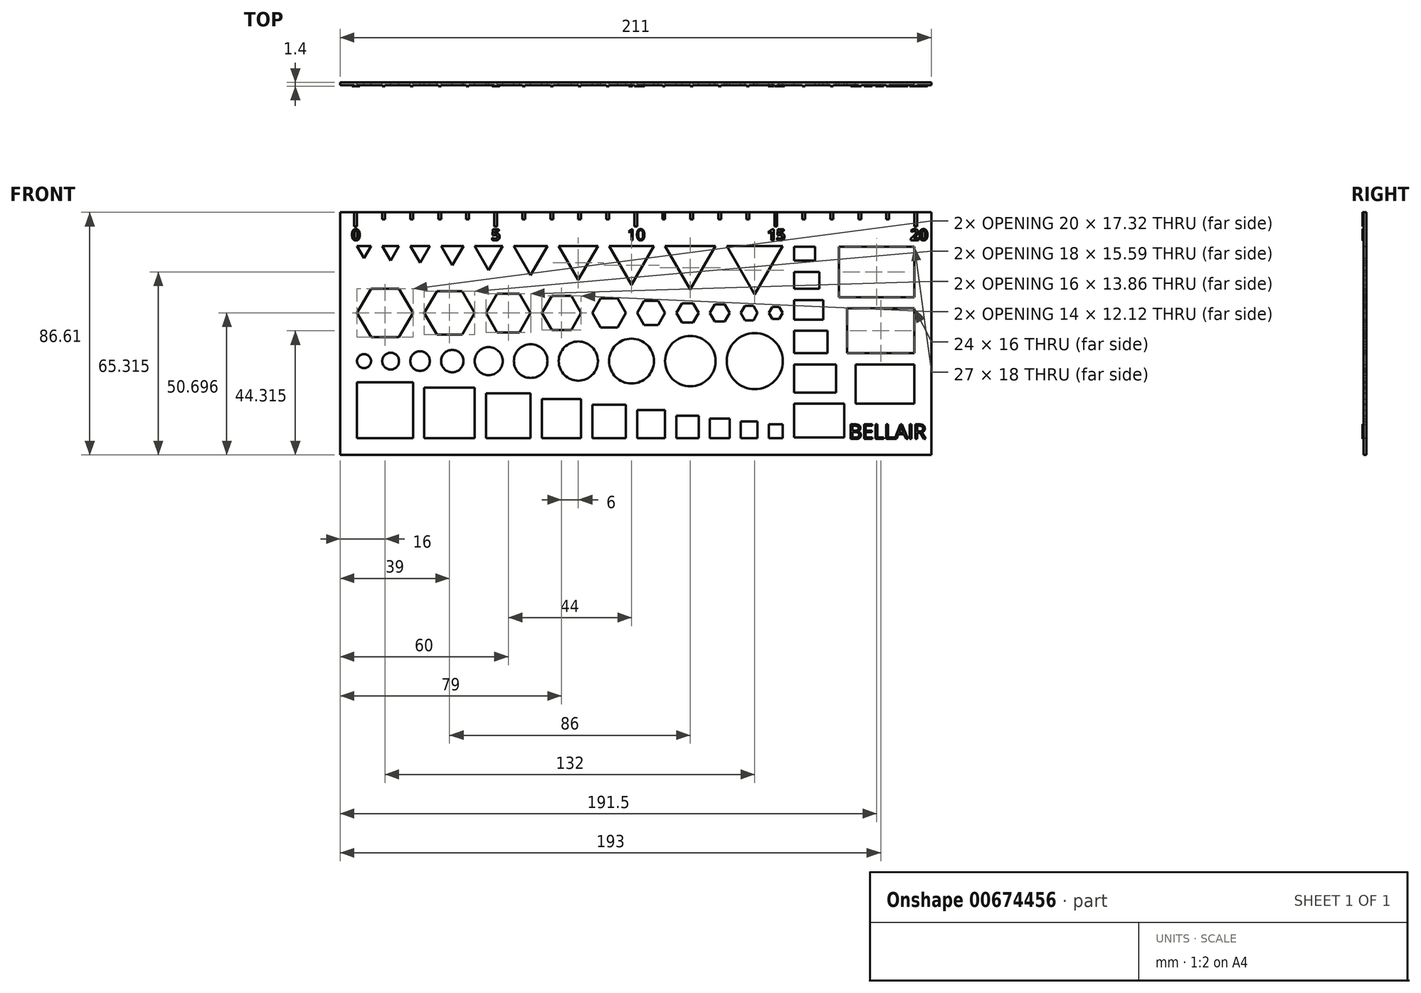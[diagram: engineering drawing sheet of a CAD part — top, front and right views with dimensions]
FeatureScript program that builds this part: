
annotation { "Feature Type Name" : "Feature", "Feature Type Description" : "" }
export const myFeature = defineFeature(function(context is Context, id is Id, definition is map)
    precondition{}
    {
        {
            var Q0;
            Q0=qCreatedBy(makeId("Front.planeOp"),FACE);
            var sketch = newSketch(context, id + "F0", { "sketchPlane" : qUnion([Q0])});
            skLineSegment(sketch, "E0.bottom", {"start": v(0, 0) * mm, "end": v(20, 0) * mm});
            skLineSegment(sketch, "E0.top", {"start": v(0, 20) * mm, "end": v(20, 20) * mm});
            skLineSegment(sketch, "E0.left", {"start": v(0, 0) * mm, "end": v(0, 20) * mm});
            skLineSegment(sketch, "E0.right", {"start": v(20, 0) * mm, "end": v(20, 20) * mm});
            skLineSegment(sketch, "E1.bottom", {"start": v(24, 0) * mm, "end": v(42, 0) * mm});
            skLineSegment(sketch, "E1.top", {"start": v(24, 18) * mm, "end": v(42, 18) * mm});
            skLineSegment(sketch, "E1.left", {"start": v(24, 0) * mm, "end": v(24, 18) * mm});
            skLineSegment(sketch, "E1.right", {"start": v(42, 0) * mm, "end": v(42, 18) * mm});
            skLineSegment(sketch, "E2.bottom", {"start": v(46, 0) * mm, "end": v(62, 0) * mm});
            skLineSegment(sketch, "E2.top", {"start": v(46, 16) * mm, "end": v(62, 16) * mm});
            skLineSegment(sketch, "E2.left", {"start": v(46, 0) * mm, "end": v(46, 16) * mm});
            skLineSegment(sketch, "E2.right", {"start": v(62, 0) * mm, "end": v(62, 16) * mm});
            skLineSegment(sketch, "E3.bottom", {"start": v(66, 0) * mm, "end": v(80, 0) * mm});
            skLineSegment(sketch, "E3.top", {"start": v(66, 14) * mm, "end": v(80, 14) * mm});
            skLineSegment(sketch, "E3.left", {"start": v(66, 0) * mm, "end": v(66, 14) * mm});
            skLineSegment(sketch, "E3.right", {"start": v(80, 0) * mm, "end": v(80, 14) * mm});
            skLineSegment(sketch, "E4.bottom", {"start": v(84, 0) * mm, "end": v(96, 0) * mm});
            skLineSegment(sketch, "E4.top", {"start": v(84, 12) * mm, "end": v(96, 12) * mm});
            skLineSegment(sketch, "E4.left", {"start": v(84, 0) * mm, "end": v(84, 12) * mm});
            skLineSegment(sketch, "E4.right", {"start": v(96, 0) * mm, "end": v(96, 12) * mm});
            skLineSegment(sketch, "E5.bottom", {"start": v(100, 0) * mm, "end": v(110, 0) * mm});
            skLineSegment(sketch, "E5.top", {"start": v(100, 10) * mm, "end": v(110, 10) * mm});
            skLineSegment(sketch, "E5.left", {"start": v(100, 0) * mm, "end": v(100, 10) * mm});
            skLineSegment(sketch, "E5.right", {"start": v(110, 0) * mm, "end": v(110, 10) * mm});
            skLineSegment(sketch, "E6.bottom", {"start": v(114, 0) * mm, "end": v(122, 0) * mm});
            skLineSegment(sketch, "E6.top", {"start": v(114, 8) * mm, "end": v(122, 8) * mm});
            skLineSegment(sketch, "E6.left", {"start": v(114, 0) * mm, "end": v(114, 8) * mm});
            skLineSegment(sketch, "E6.right", {"start": v(122, 0) * mm, "end": v(122, 8) * mm});
            skLineSegment(sketch, "E7.bottom", {"start": v(126, 0) * mm, "end": v(133, 0) * mm});
            skLineSegment(sketch, "E7.top", {"start": v(126, 7) * mm, "end": v(133, 7) * mm});
            skLineSegment(sketch, "E7.left", {"start": v(126, 0) * mm, "end": v(126, 7) * mm});
            skLineSegment(sketch, "E7.right", {"start": v(133, 0) * mm, "end": v(133, 7) * mm});
            skLineSegment(sketch, "E8.bottom", {"start": v(137, 0) * mm, "end": v(143, 0) * mm});
            skLineSegment(sketch, "E8.top", {"start": v(137, 6) * mm, "end": v(143, 6) * mm});
            skLineSegment(sketch, "E8.left", {"start": v(137, 0) * mm, "end": v(137, 6) * mm});
            skLineSegment(sketch, "E8.right", {"start": v(143, 0) * mm, "end": v(143, 6) * mm});
            skLineSegment(sketch, "E9.bottom", {"start": v(147, 0) * mm, "end": v(152, 0) * mm});
            skLineSegment(sketch, "E9.top", {"start": v(147, 5) * mm, "end": v(152, 5) * mm});
            skLineSegment(sketch, "E9.left", {"start": v(147, 0) * mm, "end": v(147, 5) * mm});
            skLineSegment(sketch, "E9.right", {"start": v(152, 0) * mm, "end": v(152, 5) * mm});
            skCircle(sketch, "E10", {"center": v(2.5, 27.5) * mm, "radius": 2.5 * mm});
            skCircle(sketch, "E11", {"center": v(12, 27.5) * mm, "radius": 3 * mm});
            skCircle(sketch, "E12", {"center": v(22.5, 27.5) * mm, "radius": 3.5 * mm});
            skCircle(sketch, "E13", {"center": v(34, 27.5) * mm, "radius": 4 * mm});
            skCircle(sketch, "E14", {"center": v(47, 27.5) * mm, "radius": 5 * mm});
            skCircle(sketch, "E15", {"center": v(62, 27.5) * mm, "radius": 6 * mm});
            skCircle(sketch, "E16", {"center": v(79, 27.5) * mm, "radius": 7 * mm});
            skCircle(sketch, "E17", {"center": v(98, 27.5) * mm, "radius": 8 * mm});
            skCircle(sketch, "E18", {"center": v(119, 27.5) * mm, "radius": 9 * mm});
            skCircle(sketch, "E19", {"center": v(142, 27.5) * mm, "radius": 10 * mm});
            skCircle(sketch, "E20.cCircle", {"center": v(10, 44.7) * mm, "radius": 8.66 * mm, "construction": true});
            skLineSegment(sketch, "E20.0", {"start": v(5, 53.36) * mm, "end": v(15, 53.36) * mm});
            skLineSegment(sketch, "E20.1", {"start": v(15, 53.36) * mm, "end": v(20, 44.7) * mm});
            skLineSegment(sketch, "E20.2", {"start": v(20, 44.7) * mm, "end": v(15, 36.04) * mm});
            skLineSegment(sketch, "E20.3", {"start": v(15, 36.04) * mm, "end": v(5, 36.04) * mm});
            skLineSegment(sketch, "E20.4", {"start": v(5, 36.04) * mm, "end": v(0, 44.7) * mm});
            skLineSegment(sketch, "E20.5", {"start": v(0, 44.7) * mm, "end": v(5, 53.36) * mm});
            skPoint(sketch, "E20.0.midPoint", {"position": v(10, 53.36) * mm});
            skCircle(sketch, "E21.cCircle", {"center": v(33, 44.7) * mm, "radius": 7.8 * mm, "construction": true});
            skLineSegment(sketch, "E21.0", {"start": v(37.5, 36.9) * mm, "end": v(28.5, 36.9) * mm});
            skLineSegment(sketch, "E21.1", {"start": v(28.5, 36.9) * mm, "end": v(24, 44.7) * mm});
            skLineSegment(sketch, "E21.2", {"start": v(24, 44.7) * mm, "end": v(28.5, 52.5) * mm});
            skLineSegment(sketch, "E21.3", {"start": v(28.5, 52.5) * mm, "end": v(37.5, 52.5) * mm});
            skLineSegment(sketch, "E21.4", {"start": v(37.5, 52.5) * mm, "end": v(42, 44.7) * mm});
            skLineSegment(sketch, "E21.5", {"start": v(42, 44.7) * mm, "end": v(37.5, 36.9) * mm});
            skPoint(sketch, "E21.0.midPoint", {"position": v(33, 36.9) * mm});
            skCircle(sketch, "E22.cCircle", {"center": v(54, 44.7) * mm, "radius": 6.93 * mm, "construction": true});
            skLineSegment(sketch, "E22.0", {"start": v(50, 51.62) * mm, "end": v(58, 51.62) * mm});
            skLineSegment(sketch, "E22.1", {"start": v(58, 51.62) * mm, "end": v(62, 44.7) * mm});
            skLineSegment(sketch, "E22.2", {"start": v(62, 44.7) * mm, "end": v(58, 37.77) * mm});
            skLineSegment(sketch, "E22.3", {"start": v(58, 37.77) * mm, "end": v(50, 37.77) * mm});
            skLineSegment(sketch, "E22.4", {"start": v(50, 37.77) * mm, "end": v(46, 44.7) * mm});
            skLineSegment(sketch, "E22.5", {"start": v(46, 44.7) * mm, "end": v(50, 51.62) * mm});
            skPoint(sketch, "E22.0.midPoint", {"position": v(54, 51.62) * mm});
            skCircle(sketch, "E23.cCircle", {"center": v(73, 44.7) * mm, "radius": 6.06 * mm, "construction": true});
            skLineSegment(sketch, "E23.0", {"start": v(69.5, 50.76) * mm, "end": v(76.5, 50.76) * mm});
            skLineSegment(sketch, "E23.1", {"start": v(76.5, 50.76) * mm, "end": v(80, 44.7) * mm});
            skLineSegment(sketch, "E23.2", {"start": v(80, 44.7) * mm, "end": v(76.5, 38.63) * mm});
            skLineSegment(sketch, "E23.3", {"start": v(76.5, 38.63) * mm, "end": v(69.5, 38.63) * mm});
            skLineSegment(sketch, "E23.4", {"start": v(69.5, 38.63) * mm, "end": v(66, 44.7) * mm});
            skLineSegment(sketch, "E23.5", {"start": v(66, 44.7) * mm, "end": v(69.5, 50.76) * mm});
            skPoint(sketch, "E23.0.midPoint", {"position": v(73, 50.76) * mm});
            skCircle(sketch, "E24.cCircle", {"center": v(90, 44.7) * mm, "radius": 5.2 * mm, "construction": true});
            skLineSegment(sketch, "E24.0", {"start": v(87, 49.9) * mm, "end": v(93, 49.9) * mm});
            skLineSegment(sketch, "E24.1", {"start": v(93, 49.9) * mm, "end": v(96, 44.7) * mm});
            skLineSegment(sketch, "E24.2", {"start": v(96, 44.7) * mm, "end": v(93, 39.5) * mm});
            skLineSegment(sketch, "E24.3", {"start": v(93, 39.5) * mm, "end": v(87, 39.5) * mm});
            skLineSegment(sketch, "E24.4", {"start": v(87, 39.5) * mm, "end": v(84, 44.7) * mm});
            skLineSegment(sketch, "E24.5", {"start": v(84, 44.7) * mm, "end": v(87, 49.9) * mm});
            skPoint(sketch, "E24.0.midPoint", {"position": v(90, 49.9) * mm});
            skCircle(sketch, "E25.cCircle", {"center": v(105, 44.7) * mm, "radius": 4.33 * mm, "construction": true});
            skLineSegment(sketch, "E25.0", {"start": v(102.5, 49.03) * mm, "end": v(107.5, 49.03) * mm});
            skLineSegment(sketch, "E25.1", {"start": v(107.5, 49.03) * mm, "end": v(110, 44.7) * mm});
            skLineSegment(sketch, "E25.2", {"start": v(110, 44.7) * mm, "end": v(107.5, 40.37) * mm});
            skLineSegment(sketch, "E25.3", {"start": v(107.5, 40.37) * mm, "end": v(102.5, 40.37) * mm});
            skLineSegment(sketch, "E25.4", {"start": v(102.5, 40.37) * mm, "end": v(100, 44.7) * mm});
            skLineSegment(sketch, "E25.5", {"start": v(100, 44.7) * mm, "end": v(102.5, 49.03) * mm});
            skPoint(sketch, "E25.0.midPoint", {"position": v(105, 49.03) * mm});
            skCircle(sketch, "E26.cCircle", {"center": v(118, 44.7) * mm, "radius": 3.46 * mm, "construction": true});
            skLineSegment(sketch, "E26.0", {"start": v(116, 48.16) * mm, "end": v(120, 48.16) * mm});
            skLineSegment(sketch, "E26.1", {"start": v(120, 48.16) * mm, "end": v(122, 44.7) * mm});
            skLineSegment(sketch, "E26.2", {"start": v(122, 44.7) * mm, "end": v(120, 41.23) * mm});
            skLineSegment(sketch, "E26.3", {"start": v(120, 41.23) * mm, "end": v(116, 41.23) * mm});
            skLineSegment(sketch, "E26.4", {"start": v(116, 41.23) * mm, "end": v(114, 44.7) * mm});
            skLineSegment(sketch, "E26.5", {"start": v(114, 44.7) * mm, "end": v(116, 48.16) * mm});
            skPoint(sketch, "E26.0.midPoint", {"position": v(118, 48.16) * mm});
            skCircle(sketch, "E27.cCircle", {"center": v(129.5, 44.7) * mm, "radius": 3.03 * mm, "construction": true});
            skLineSegment(sketch, "E27.0", {"start": v(127.75, 47.73) * mm, "end": v(131.25, 47.73) * mm});
            skLineSegment(sketch, "E27.1", {"start": v(131.25, 47.73) * mm, "end": v(133, 44.7) * mm});
            skLineSegment(sketch, "E27.2", {"start": v(133, 44.7) * mm, "end": v(131.25, 41.67) * mm});
            skLineSegment(sketch, "E27.3", {"start": v(131.25, 41.67) * mm, "end": v(127.75, 41.67) * mm});
            skLineSegment(sketch, "E27.4", {"start": v(127.75, 41.67) * mm, "end": v(126, 44.7) * mm});
            skLineSegment(sketch, "E27.5", {"start": v(126, 44.7) * mm, "end": v(127.75, 47.73) * mm});
            skPoint(sketch, "E27.0.midPoint", {"position": v(129.5, 47.73) * mm});
            skCircle(sketch, "E28.cCircle", {"center": v(140, 44.7) * mm, "radius": 2.6 * mm, "construction": true});
            skLineSegment(sketch, "E28.0", {"start": v(138.5, 47.3) * mm, "end": v(141.5, 47.3) * mm});
            skLineSegment(sketch, "E28.1", {"start": v(141.5, 47.3) * mm, "end": v(143, 44.7) * mm});
            skLineSegment(sketch, "E28.2", {"start": v(143, 44.7) * mm, "end": v(141.5, 42.1) * mm});
            skLineSegment(sketch, "E28.3", {"start": v(141.5, 42.1) * mm, "end": v(138.5, 42.1) * mm});
            skLineSegment(sketch, "E28.4", {"start": v(138.5, 42.1) * mm, "end": v(137, 44.7) * mm});
            skLineSegment(sketch, "E28.5", {"start": v(137, 44.7) * mm, "end": v(138.5, 47.3) * mm});
            skPoint(sketch, "E28.0.midPoint", {"position": v(140, 47.3) * mm});
            skCircle(sketch, "E29.cCircle", {"center": v(149.5, 44.7) * mm, "radius": 2.17 * mm, "construction": true});
            skLineSegment(sketch, "E29.0", {"start": v(148.25, 46.86) * mm, "end": v(150.75, 46.86) * mm});
            skLineSegment(sketch, "E29.1", {"start": v(150.75, 46.86) * mm, "end": v(152, 44.7) * mm});
            skLineSegment(sketch, "E29.2", {"start": v(152, 44.7) * mm, "end": v(150.75, 42.53) * mm});
            skLineSegment(sketch, "E29.3", {"start": v(150.75, 42.53) * mm, "end": v(148.25, 42.53) * mm});
            skLineSegment(sketch, "E29.4", {"start": v(148.25, 42.53) * mm, "end": v(147, 44.7) * mm});
            skLineSegment(sketch, "E29.5", {"start": v(147, 44.7) * mm, "end": v(148.25, 46.86) * mm});
            skPoint(sketch, "E29.0.midPoint", {"position": v(149.5, 46.86) * mm});
            skCircle(sketch, "E30.cCircle", {"center": v(2.5, 67.17) * mm, "radius": 1.44 * mm, "construction": true});
            skLineSegment(sketch, "E30.0", {"start": v(0, 68.61) * mm, "end": v(5, 68.61) * mm});
            skLineSegment(sketch, "E30.1", {"start": v(5, 68.61) * mm, "end": v(2.5, 64.28) * mm});
            skLineSegment(sketch, "E30.2", {"start": v(2.5, 64.28) * mm, "end": v(0, 68.61) * mm});
            skPoint(sketch, "E30.0.midPoint", {"position": v(2.5, 68.61) * mm});
            skCircle(sketch, "E31.cCircle", {"center": v(12, 66.88) * mm, "radius": 1.73 * mm, "construction": true});
            skLineSegment(sketch, "E31.0", {"start": v(9, 68.61) * mm, "end": v(15, 68.61) * mm});
            skLineSegment(sketch, "E31.1", {"start": v(15, 68.61) * mm, "end": v(12, 63.42) * mm});
            skLineSegment(sketch, "E31.2", {"start": v(12, 63.42) * mm, "end": v(9, 68.61) * mm});
            skPoint(sketch, "E31.0.midPoint", {"position": v(12, 68.61) * mm});
            skCircle(sketch, "E32.cCircle", {"center": v(22.5, 66.6) * mm, "radius": 2.02 * mm, "construction": true});
            skLineSegment(sketch, "E32.0", {"start": v(19, 68.61) * mm, "end": v(26, 68.61) * mm});
            skLineSegment(sketch, "E32.1", {"start": v(26, 68.61) * mm, "end": v(22.5, 62.55) * mm});
            skLineSegment(sketch, "E32.2", {"start": v(22.5, 62.55) * mm, "end": v(19, 68.61) * mm});
            skPoint(sketch, "E32.0.midPoint", {"position": v(22.5, 68.61) * mm});
            skCircle(sketch, "E33.cCircle", {"center": v(34, 66.3) * mm, "radius": 2.3 * mm, "construction": true});
            skLineSegment(sketch, "E33.0", {"start": v(30, 68.61) * mm, "end": v(38, 68.61) * mm});
            skLineSegment(sketch, "E33.1", {"start": v(38, 68.61) * mm, "end": v(34, 61.69) * mm});
            skLineSegment(sketch, "E33.2", {"start": v(34, 61.69) * mm, "end": v(30, 68.61) * mm});
            skPoint(sketch, "E33.0.midPoint", {"position": v(34, 68.61) * mm});
            skCircle(sketch, "E34.cCircle", {"center": v(47, 65.73) * mm, "radius": 2.89 * mm, "construction": true});
            skLineSegment(sketch, "E34.0", {"start": v(42, 68.61) * mm, "end": v(52, 68.61) * mm});
            skLineSegment(sketch, "E34.1", {"start": v(52, 68.61) * mm, "end": v(47, 59.95) * mm});
            skLineSegment(sketch, "E34.2", {"start": v(47, 59.95) * mm, "end": v(42, 68.61) * mm});
            skPoint(sketch, "E34.0.midPoint", {"position": v(47, 68.61) * mm});
            skCircle(sketch, "E35.cCircle", {"center": v(79, 64.57) * mm, "radius": 4.04 * mm, "construction": true});
            skLineSegment(sketch, "E35.0", {"start": v(72, 68.61) * mm, "end": v(86, 68.61) * mm});
            skLineSegment(sketch, "E35.1", {"start": v(86, 68.61) * mm, "end": v(79, 56.5) * mm});
            skLineSegment(sketch, "E35.2", {"start": v(79, 56.5) * mm, "end": v(72, 68.61) * mm});
            skPoint(sketch, "E35.0.midPoint", {"position": v(79, 68.61) * mm});
            skCircle(sketch, "E36.cCircle", {"center": v(98, 64) * mm, "radius": 4.62 * mm, "construction": true});
            skLineSegment(sketch, "E36.0", {"start": v(90, 68.61) * mm, "end": v(106, 68.61) * mm});
            skLineSegment(sketch, "E36.1", {"start": v(106, 68.61) * mm, "end": v(98, 54.76) * mm});
            skLineSegment(sketch, "E36.2", {"start": v(98, 54.76) * mm, "end": v(90, 68.61) * mm});
            skPoint(sketch, "E36.0.midPoint", {"position": v(98, 68.61) * mm});
            skCircle(sketch, "E37.cCircle", {"center": v(119, 63.42) * mm, "radius": 5.2 * mm, "construction": true});
            skLineSegment(sketch, "E37.0", {"start": v(110, 68.61) * mm, "end": v(128, 68.61) * mm});
            skLineSegment(sketch, "E37.1", {"start": v(128, 68.61) * mm, "end": v(119, 53.03) * mm});
            skLineSegment(sketch, "E37.2", {"start": v(119, 53.03) * mm, "end": v(110, 68.61) * mm});
            skPoint(sketch, "E37.0.midPoint", {"position": v(119, 68.61) * mm});
            skCircle(sketch, "E38.cCircle", {"center": v(62, 65.15) * mm, "radius": 3.46 * mm, "construction": true});
            skLineSegment(sketch, "E38.0", {"start": v(56, 68.61) * mm, "end": v(68, 68.61) * mm});
            skLineSegment(sketch, "E38.1", {"start": v(68, 68.61) * mm, "end": v(62, 58.22) * mm});
            skLineSegment(sketch, "E38.2", {"start": v(62, 58.22) * mm, "end": v(56, 68.61) * mm});
            skPoint(sketch, "E38.0.midPoint", {"position": v(62, 68.61) * mm});
            skCircle(sketch, "E39.cCircle", {"center": v(142, 62.84) * mm, "radius": 5.77 * mm, "construction": true});
            skLineSegment(sketch, "E39.0", {"start": v(132, 68.61) * mm, "end": v(152, 68.61) * mm});
            skLineSegment(sketch, "E39.1", {"start": v(152, 68.61) * mm, "end": v(142, 51.3) * mm});
            skLineSegment(sketch, "E39.2", {"start": v(142, 51.3) * mm, "end": v(132, 68.61) * mm});
            skPoint(sketch, "E39.0.midPoint", {"position": v(142, 68.61) * mm});
            skLineSegment(sketch, "E40", {"start": v(156, 68.61) * mm, "end": v(156, 0) * mm});
            skLineSegment(sketch, "E41.bottom", {"start": v(156, 68.31) * mm, "end": v(163.5, 68.31) * mm});
            skLineSegment(sketch, "E41.top", {"start": v(156, 63.31) * mm, "end": v(163.5, 63.31) * mm});
            skLineSegment(sketch, "E41.left", {"start": v(156, 68.31) * mm, "end": v(156, 63.31) * mm});
            skLineSegment(sketch, "E41.right", {"start": v(163.5, 68.31) * mm, "end": v(163.5, 63.31) * mm});
            skLineSegment(sketch, "E42.bottom", {"start": v(156, 59.31) * mm, "end": v(165, 59.31) * mm});
            skLineSegment(sketch, "E42.top", {"start": v(156, 53.31) * mm, "end": v(165, 53.31) * mm});
            skLineSegment(sketch, "E42.left", {"start": v(156, 59.31) * mm, "end": v(156, 53.31) * mm});
            skLineSegment(sketch, "E42.right", {"start": v(165, 59.31) * mm, "end": v(165, 53.31) * mm});
            skLineSegment(sketch, "E43.bottom", {"start": v(156, 49.31) * mm, "end": v(166.5, 49.31) * mm});
            skLineSegment(sketch, "E43.top", {"start": v(156, 42.31) * mm, "end": v(166.5, 42.31) * mm});
            skLineSegment(sketch, "E43.left", {"start": v(156, 49.31) * mm, "end": v(156, 42.31) * mm});
            skLineSegment(sketch, "E43.right", {"start": v(166.5, 49.31) * mm, "end": v(166.5, 42.31) * mm});
            skLineSegment(sketch, "E44.bottom", {"start": v(156, 38.31) * mm, "end": v(168, 38.31) * mm});
            skLineSegment(sketch, "E44.top", {"start": v(156, 30.31) * mm, "end": v(168, 30.31) * mm});
            skLineSegment(sketch, "E44.left", {"start": v(156, 38.31) * mm, "end": v(156, 30.31) * mm});
            skLineSegment(sketch, "E44.right", {"start": v(168, 38.31) * mm, "end": v(168, 30.31) * mm});
            skLineSegment(sketch, "E45.bottom", {"start": v(156, 26.31) * mm, "end": v(171, 26.31) * mm});
            skLineSegment(sketch, "E45.top", {"start": v(156, 16.31) * mm, "end": v(171, 16.31) * mm});
            skLineSegment(sketch, "E45.left", {"start": v(156, 26.31) * mm, "end": v(156, 16.31) * mm});
            skLineSegment(sketch, "E45.right", {"start": v(171, 26.31) * mm, "end": v(171, 16.31) * mm});
            skLineSegment(sketch, "E46.bottom", {"start": v(156, 12.31) * mm, "end": v(174, 12.31) * mm});
            skLineSegment(sketch, "E46.top", {"start": v(156, 0.31) * mm, "end": v(174, 0.31) * mm});
            skLineSegment(sketch, "E46.left", {"start": v(156, 12.31) * mm, "end": v(156, 0.31) * mm});
            skLineSegment(sketch, "E46.right", {"start": v(174, 12.31) * mm, "end": v(174, 0.31) * mm});
            skLineSegment(sketch, "E47.bottom", {"start": v(199, 68.31) * mm, "end": v(172, 68.31) * mm});
            skLineSegment(sketch, "E47.top", {"start": v(199, 50.31) * mm, "end": v(172, 50.31) * mm});
            skLineSegment(sketch, "E47.left", {"start": v(199, 68.31) * mm, "end": v(199, 50.31) * mm});
            skLineSegment(sketch, "E47.right", {"start": v(172, 68.31) * mm, "end": v(172, 50.31) * mm});
            skLineSegment(sketch, "E48.bottom", {"start": v(199, 46.31) * mm, "end": v(175, 46.31) * mm});
            skLineSegment(sketch, "E48.top", {"start": v(199, 30.31) * mm, "end": v(175, 30.31) * mm});
            skLineSegment(sketch, "E48.left", {"start": v(199, 46.31) * mm, "end": v(199, 30.31) * mm});
            skLineSegment(sketch, "E48.right", {"start": v(175, 46.31) * mm, "end": v(175, 30.31) * mm});
            skLineSegment(sketch, "E49.bottom", {"start": v(199, 26.31) * mm, "end": v(178, 26.31) * mm});
            skLineSegment(sketch, "E49.top", {"start": v(199, 12.31) * mm, "end": v(178, 12.31) * mm});
            skLineSegment(sketch, "E49.left", {"start": v(199, 26.31) * mm, "end": v(199, 12.31) * mm});
            skLineSegment(sketch, "E49.right", {"start": v(178, 26.31) * mm, "end": v(178, 12.31) * mm});
            skLineSegment(sketch, "E50.bottom", {"start": v(-6, 80.61) * mm, "end": v(205, 80.61) * mm});
            skLineSegment(sketch, "E50.top", {"start": v(-6, -6) * mm, "end": v(205, -6) * mm});
            skLineSegment(sketch, "E50.left", {"start": v(-6, 80.61) * mm, "end": v(-6, -6) * mm});
            skLineSegment(sketch, "E50.right", {"start": v(205, 80.61) * mm, "end": v(205, -6) * mm});
            skSolve(sketch);
        }
        {
            var Q0;
            Q0=qSketchRegion(id+"F0",true);
            extrude(context, id + "F1", {"entities" : qUnion([Q0]), "depth" : 1 * mm, "offsetDistance" : 25 * mm});
        }
        {
            var Q0;
            Q0=makeQuery(id+"F1.opExtrude","CAP_FACE",FACE,{"disambiguationData":[OSD([sQuery(id+"F0.wireOp",EDGE,"E0.bottom"),sQuery(id+"F0.wireOp",EDGE,"E0.top"),sQuery(id+"F0.wireOp",EDGE,"E0.left"),sQuery(id+"F0.wireOp",EDGE,"E0.right"),sQuery(id+"F0.wireOp",EDGE,"E1.bottom"),sQuery(id+"F0.wireOp",EDGE,"E1.top"),sQuery(id+"F0.wireOp",EDGE,"E1.left"),sQuery(id+"F0.wireOp",EDGE,"E1.right"),sQuery(id+"F0.wireOp",EDGE,"E2.bottom"),sQuery(id+"F0.wireOp",EDGE,"E2.top"),sQuery(id+"F0.wireOp",EDGE,"E2.left"),sQuery(id+"F0.wireOp",EDGE,"E2.right"),sQuery(id+"F0.wireOp",EDGE,"E3.bottom"),sQuery(id+"F0.wireOp",EDGE,"E3.top"),sQuery(id+"F0.wireOp",EDGE,"E3.left"),sQuery(id+"F0.wireOp",EDGE,"E3.right"),sQuery(id+"F0.wireOp",EDGE,"E4.bottom"),sQuery(id+"F0.wireOp",EDGE,"E4.top"),sQuery(id+"F0.wireOp",EDGE,"E4.left"),sQuery(id+"F0.wireOp",EDGE,"E4.right"),sQuery(id+"F0.wireOp",EDGE,"E5.bottom"),sQuery(id+"F0.wireOp",EDGE,"E5.top"),sQuery(id+"F0.wireOp",EDGE,"E5.left"),sQuery(id+"F0.wireOp",EDGE,"E5.right"),sQuery(id+"F0.wireOp",EDGE,"E6.bottom"),sQuery(id+"F0.wireOp",EDGE,"E6.top"),sQuery(id+"F0.wireOp",EDGE,"E6.left"),sQuery(id+"F0.wireOp",EDGE,"E6.right"),sQuery(id+"F0.wireOp",EDGE,"E7.bottom"),sQuery(id+"F0.wireOp",EDGE,"E7.top"),sQuery(id+"F0.wireOp",EDGE,"E7.left"),sQuery(id+"F0.wireOp",EDGE,"E7.right"),sQuery(id+"F0.wireOp",EDGE,"E8.bottom"),sQuery(id+"F0.wireOp",EDGE,"E8.top"),sQuery(id+"F0.wireOp",EDGE,"E8.left"),sQuery(id+"F0.wireOp",EDGE,"E8.right"),sQuery(id+"F0.wireOp",EDGE,"E9.bottom"),sQuery(id+"F0.wireOp",EDGE,"E9.top"),sQuery(id+"F0.wireOp",EDGE,"E9.left"),sQuery(id+"F0.wireOp",EDGE,"E9.right"),sQuery(id+"F0.wireOp",EDGE,"E10"),sQuery(id+"F0.wireOp",EDGE,"E11"),sQuery(id+"F0.wireOp",EDGE,"E12"),sQuery(id+"F0.wireOp",EDGE,"E13"),sQuery(id+"F0.wireOp",EDGE,"E14"),sQuery(id+"F0.wireOp",EDGE,"E15"),sQuery(id+"F0.wireOp",EDGE,"E16"),sQuery(id+"F0.wireOp",EDGE,"E17"),sQuery(id+"F0.wireOp",EDGE,"E18"),sQuery(id+"F0.wireOp",EDGE,"E19"),sQuery(id+"F0.wireOp",EDGE,"E20.0"),sQuery(id+"F0.wireOp",EDGE,"E20.1"),sQuery(id+"F0.wireOp",EDGE,"E20.2"),sQuery(id+"F0.wireOp",EDGE,"E20.3"),sQuery(id+"F0.wireOp",EDGE,"E20.4"),sQuery(id+"F0.wireOp",EDGE,"E20.5"),sQuery(id+"F0.wireOp",EDGE,"E21.0"),sQuery(id+"F0.wireOp",EDGE,"E21.1"),sQuery(id+"F0.wireOp",EDGE,"E21.2"),sQuery(id+"F0.wireOp",EDGE,"E21.3"),sQuery(id+"F0.wireOp",EDGE,"E21.4"),sQuery(id+"F0.wireOp",EDGE,"E21.5"),sQuery(id+"F0.wireOp",EDGE,"E22.0"),sQuery(id+"F0.wireOp",EDGE,"E22.1"),sQuery(id+"F0.wireOp",EDGE,"E22.2"),sQuery(id+"F0.wireOp",EDGE,"E22.3"),sQuery(id+"F0.wireOp",EDGE,"E22.4"),sQuery(id+"F0.wireOp",EDGE,"E22.5"),sQuery(id+"F0.wireOp",EDGE,"E23.0"),sQuery(id+"F0.wireOp",EDGE,"E23.1"),sQuery(id+"F0.wireOp",EDGE,"E23.2"),sQuery(id+"F0.wireOp",EDGE,"E23.3"),sQuery(id+"F0.wireOp",EDGE,"E23.4"),sQuery(id+"F0.wireOp",EDGE,"E23.5"),sQuery(id+"F0.wireOp",EDGE,"E24.0"),sQuery(id+"F0.wireOp",EDGE,"E24.1"),sQuery(id+"F0.wireOp",EDGE,"E24.2"),sQuery(id+"F0.wireOp",EDGE,"E24.3"),sQuery(id+"F0.wireOp",EDGE,"E24.4"),sQuery(id+"F0.wireOp",EDGE,"E24.5"),sQuery(id+"F0.wireOp",EDGE,"E25.0"),sQuery(id+"F0.wireOp",EDGE,"E25.1"),sQuery(id+"F0.wireOp",EDGE,"E25.2"),sQuery(id+"F0.wireOp",EDGE,"E25.3"),sQuery(id+"F0.wireOp",EDGE,"E25.4"),sQuery(id+"F0.wireOp",EDGE,"E25.5"),sQuery(id+"F0.wireOp",EDGE,"E26.0"),sQuery(id+"F0.wireOp",EDGE,"E26.1"),sQuery(id+"F0.wireOp",EDGE,"E26.2"),sQuery(id+"F0.wireOp",EDGE,"E26.3"),sQuery(id+"F0.wireOp",EDGE,"E26.4"),sQuery(id+"F0.wireOp",EDGE,"E26.5"),sQuery(id+"F0.wireOp",EDGE,"E27.0"),sQuery(id+"F0.wireOp",EDGE,"E27.1"),sQuery(id+"F0.wireOp",EDGE,"E27.2"),sQuery(id+"F0.wireOp",EDGE,"E27.3"),sQuery(id+"F0.wireOp",EDGE,"E27.4"),sQuery(id+"F0.wireOp",EDGE,"E27.5"),sQuery(id+"F0.wireOp",EDGE,"E28.0"),sQuery(id+"F0.wireOp",EDGE,"E28.1"),sQuery(id+"F0.wireOp",EDGE,"E28.2"),sQuery(id+"F0.wireOp",EDGE,"E28.3"),sQuery(id+"F0.wireOp",EDGE,"E28.4"),sQuery(id+"F0.wireOp",EDGE,"E28.5"),sQuery(id+"F0.wireOp",EDGE,"E29.0"),sQuery(id+"F0.wireOp",EDGE,"E29.1"),sQuery(id+"F0.wireOp",EDGE,"E29.2"),sQuery(id+"F0.wireOp",EDGE,"E29.3"),sQuery(id+"F0.wireOp",EDGE,"E29.4"),sQuery(id+"F0.wireOp",EDGE,"E29.5"),sQuery(id+"F0.wireOp",EDGE,"E30.0"),sQuery(id+"F0.wireOp",EDGE,"E30.1"),sQuery(id+"F0.wireOp",EDGE,"E30.2"),sQuery(id+"F0.wireOp",EDGE,"E31.0"),sQuery(id+"F0.wireOp",EDGE,"E31.1"),sQuery(id+"F0.wireOp",EDGE,"E31.2"),sQuery(id+"F0.wireOp",EDGE,"E32.0"),sQuery(id+"F0.wireOp",EDGE,"E32.1"),sQuery(id+"F0.wireOp",EDGE,"E32.2"),sQuery(id+"F0.wireOp",EDGE,"E33.0"),sQuery(id+"F0.wireOp",EDGE,"E33.1"),sQuery(id+"F0.wireOp",EDGE,"E33.2"),sQuery(id+"F0.wireOp",EDGE,"E34.0"),sQuery(id+"F0.wireOp",EDGE,"E34.1"),sQuery(id+"F0.wireOp",EDGE,"E34.2"),sQuery(id+"F0.wireOp",EDGE,"E35.0"),sQuery(id+"F0.wireOp",EDGE,"E35.1"),sQuery(id+"F0.wireOp",EDGE,"E35.2"),sQuery(id+"F0.wireOp",EDGE,"E36.0"),sQuery(id+"F0.wireOp",EDGE,"E36.1"),sQuery(id+"F0.wireOp",EDGE,"E36.2"),sQuery(id+"F0.wireOp",EDGE,"E37.0"),sQuery(id+"F0.wireOp",EDGE,"E37.1"),sQuery(id+"F0.wireOp",EDGE,"E37.2"),sQuery(id+"F0.wireOp",EDGE,"E38.0"),sQuery(id+"F0.wireOp",EDGE,"E38.1"),sQuery(id+"F0.wireOp",EDGE,"E38.2"),sQuery(id+"F0.wireOp",EDGE,"E39.0"),sQuery(id+"F0.wireOp",EDGE,"E39.1"),sQuery(id+"F0.wireOp",EDGE,"E39.2"),sQuery(id+"F0.wireOp",EDGE,"E41.bottom"),sQuery(id+"F0.wireOp",EDGE,"E41.top"),sQuery(id+"F0.wireOp",EDGE,"E41.left"),sQuery(id+"F0.wireOp",EDGE,"E41.right"),sQuery(id+"F0.wireOp",EDGE,"E42.bottom"),sQuery(id+"F0.wireOp",EDGE,"E42.top"),sQuery(id+"F0.wireOp",EDGE,"E42.left"),sQuery(id+"F0.wireOp",EDGE,"E42.right"),sQuery(id+"F0.wireOp",EDGE,"E43.bottom"),sQuery(id+"F0.wireOp",EDGE,"E43.top"),sQuery(id+"F0.wireOp",EDGE,"E43.left"),sQuery(id+"F0.wireOp",EDGE,"E43.right"),sQuery(id+"F0.wireOp",EDGE,"E44.bottom"),sQuery(id+"F0.wireOp",EDGE,"E44.top"),sQuery(id+"F0.wireOp",EDGE,"E44.left"),sQuery(id+"F0.wireOp",EDGE,"E44.right"),sQuery(id+"F0.wireOp",EDGE,"E45.bottom"),sQuery(id+"F0.wireOp",EDGE,"E45.top"),sQuery(id+"F0.wireOp",EDGE,"E45.left"),sQuery(id+"F0.wireOp",EDGE,"E45.right"),sQuery(id+"F0.wireOp",EDGE,"E46.bottom"),sQuery(id+"F0.wireOp",EDGE,"E46.top"),sQuery(id+"F0.wireOp",EDGE,"E46.left"),sQuery(id+"F0.wireOp",EDGE,"E46.right"),sQuery(id+"F0.wireOp",EDGE,"E47.bottom"),sQuery(id+"F0.wireOp",EDGE,"E47.top"),sQuery(id+"F0.wireOp",EDGE,"E47.left"),sQuery(id+"F0.wireOp",EDGE,"E47.right"),sQuery(id+"F0.wireOp",EDGE,"E48.bottom"),sQuery(id+"F0.wireOp",EDGE,"E48.top"),sQuery(id+"F0.wireOp",EDGE,"E48.left"),sQuery(id+"F0.wireOp",EDGE,"E48.right"),sQuery(id+"F0.wireOp",EDGE,"E49.bottom"),sQuery(id+"F0.wireOp",EDGE,"E49.top"),sQuery(id+"F0.wireOp",EDGE,"E49.left"),sQuery(id+"F0.wireOp",EDGE,"E49.right"),sQuery(id+"F0.wireOp",EDGE,"E50.bottom"),sQuery(id+"F0.wireOp",EDGE,"E50.top"),sQuery(id+"F0.wireOp",EDGE,"E50.left"),sQuery(id+"F0.wireOp",EDGE,"E50.right")])],"isStart":false});
            var sketch = newSketch(context, id + "F2", { "sketchPlane" : qUnion([Q0])});
            skText(sketch, "E51", { "text": "BELLAIR", "fontName": "OpenSans-Regular.ttf"});
            const initialGuessF2  = {"E51": [0.17555, -0.00031, 1, 0, 0.00528]};
            skSetInitialGuess(sketch, initialGuessF2);
            skSolve(sketch);
        }
        {
            var Q0;
            Q0=qSketchRegion(id+"F2",true);
            extrude(context, id + "F3", {"entities" : qUnion([Q0]), "operationType" : NewBodyOperationType.ADD, "depth" : 0.4 * mm, "offsetDistance" : 25 * mm});
        }
        {
            var Q0;
            {var subQ0=sQuery(id+"F0.wireOp",EDGE,"E50.right");var subQ1=sQuery(id+"F0.wireOp",EDGE,"E50.left");var subQ2=sQuery(id+"F0.wireOp",EDGE,"E50.top");var subQ3=sQuery(id+"F0.wireOp",EDGE,"E50.bottom");var subQ4=sQuery(id+"F0.wireOp",EDGE,"E49.right");var subQ5=sQuery(id+"F0.wireOp",EDGE,"E49.left");var subQ6=sQuery(id+"F0.wireOp",EDGE,"E49.top");var subQ7=sQuery(id+"F0.wireOp",EDGE,"E49.bottom");var subQ8=sQuery(id+"F0.wireOp",EDGE,"E48.right");var subQ9=sQuery(id+"F0.wireOp",EDGE,"E48.left");var subQ10=sQuery(id+"F0.wireOp",EDGE,"E48.top");var subQ11=sQuery(id+"F0.wireOp",EDGE,"E48.bottom");var subQ12=sQuery(id+"F0.wireOp",EDGE,"E47.right");var subQ13=sQuery(id+"F0.wireOp",EDGE,"E47.left");var subQ14=sQuery(id+"F0.wireOp",EDGE,"E47.top");var subQ15=sQuery(id+"F0.wireOp",EDGE,"E47.bottom");var subQ16=sQuery(id+"F0.wireOp",EDGE,"E46.right");var subQ17=sQuery(id+"F0.wireOp",EDGE,"E46.left");var subQ18=sQuery(id+"F0.wireOp",EDGE,"E46.top");var subQ19=sQuery(id+"F0.wireOp",EDGE,"E46.bottom");var subQ20=sQuery(id+"F0.wireOp",EDGE,"E45.right");var subQ21=sQuery(id+"F0.wireOp",EDGE,"E45.left");var subQ22=sQuery(id+"F0.wireOp",EDGE,"E45.top");var subQ23=sQuery(id+"F0.wireOp",EDGE,"E45.bottom");var subQ24=sQuery(id+"F0.wireOp",EDGE,"E44.right");var subQ25=sQuery(id+"F0.wireOp",EDGE,"E44.left");var subQ26=sQuery(id+"F0.wireOp",EDGE,"E44.top");var subQ27=sQuery(id+"F0.wireOp",EDGE,"E44.bottom");var subQ28=sQuery(id+"F0.wireOp",EDGE,"E43.right");var subQ29=sQuery(id+"F0.wireOp",EDGE,"E43.left");var subQ30=sQuery(id+"F0.wireOp",EDGE,"E43.top");var subQ31=sQuery(id+"F0.wireOp",EDGE,"E43.bottom");var subQ32=sQuery(id+"F0.wireOp",EDGE,"E42.right");var subQ33=sQuery(id+"F0.wireOp",EDGE,"E42.left");var subQ34=sQuery(id+"F0.wireOp",EDGE,"E42.top");var subQ35=sQuery(id+"F0.wireOp",EDGE,"E42.bottom");var subQ36=sQuery(id+"F0.wireOp",EDGE,"E41.right");var subQ37=sQuery(id+"F0.wireOp",EDGE,"E41.left");var subQ38=sQuery(id+"F0.wireOp",EDGE,"E41.top");var subQ39=sQuery(id+"F0.wireOp",EDGE,"E41.bottom");var subQ40=sQuery(id+"F0.wireOp",EDGE,"E39.2");var subQ41=sQuery(id+"F0.wireOp",EDGE,"E39.1");var subQ42=sQuery(id+"F0.wireOp",EDGE,"E39.0");var subQ43=sQuery(id+"F0.wireOp",EDGE,"E38.2");var subQ44=sQuery(id+"F0.wireOp",EDGE,"E38.1");var subQ45=sQuery(id+"F0.wireOp",EDGE,"E38.0");var subQ46=sQuery(id+"F0.wireOp",EDGE,"E37.2");var subQ47=sQuery(id+"F0.wireOp",EDGE,"E37.1");var subQ48=sQuery(id+"F0.wireOp",EDGE,"E37.0");var subQ49=sQuery(id+"F0.wireOp",EDGE,"E36.2");var subQ50=sQuery(id+"F0.wireOp",EDGE,"E36.1");var subQ51=sQuery(id+"F0.wireOp",EDGE,"E36.0");var subQ52=sQuery(id+"F0.wireOp",EDGE,"E35.2");var subQ53=sQuery(id+"F0.wireOp",EDGE,"E35.1");var subQ54=sQuery(id+"F0.wireOp",EDGE,"E35.0");var subQ55=sQuery(id+"F0.wireOp",EDGE,"E34.2");var subQ56=sQuery(id+"F0.wireOp",EDGE,"E34.1");var subQ57=sQuery(id+"F0.wireOp",EDGE,"E34.0");var subQ58=sQuery(id+"F0.wireOp",EDGE,"E33.2");var subQ59=sQuery(id+"F0.wireOp",EDGE,"E33.1");var subQ60=sQuery(id+"F0.wireOp",EDGE,"E33.0");var subQ61=sQuery(id+"F0.wireOp",EDGE,"E32.2");var subQ62=sQuery(id+"F0.wireOp",EDGE,"E32.1");var subQ63=sQuery(id+"F0.wireOp",EDGE,"E32.0");var subQ64=sQuery(id+"F0.wireOp",EDGE,"E31.2");var subQ65=sQuery(id+"F0.wireOp",EDGE,"E31.1");var subQ66=sQuery(id+"F0.wireOp",EDGE,"E31.0");var subQ67=sQuery(id+"F0.wireOp",EDGE,"E30.2");var subQ68=sQuery(id+"F0.wireOp",EDGE,"E30.1");var subQ69=sQuery(id+"F0.wireOp",EDGE,"E30.0");var subQ70=sQuery(id+"F0.wireOp",EDGE,"E29.5");var subQ71=sQuery(id+"F0.wireOp",EDGE,"E29.4");var subQ72=sQuery(id+"F0.wireOp",EDGE,"E29.3");var subQ73=sQuery(id+"F0.wireOp",EDGE,"E29.2");var subQ74=sQuery(id+"F0.wireOp",EDGE,"E29.1");var subQ75=sQuery(id+"F0.wireOp",EDGE,"E29.0");var subQ76=sQuery(id+"F0.wireOp",EDGE,"E28.5");var subQ77=sQuery(id+"F0.wireOp",EDGE,"E28.4");var subQ78=sQuery(id+"F0.wireOp",EDGE,"E28.3");var subQ79=sQuery(id+"F0.wireOp",EDGE,"E28.2");var subQ80=sQuery(id+"F0.wireOp",EDGE,"E28.1");var subQ81=sQuery(id+"F0.wireOp",EDGE,"E28.0");var subQ82=sQuery(id+"F0.wireOp",EDGE,"E27.5");var subQ83=sQuery(id+"F0.wireOp",EDGE,"E27.4");var subQ84=sQuery(id+"F0.wireOp",EDGE,"E14");var subQ85=sQuery(id+"F0.wireOp",EDGE,"E13");var subQ86=sQuery(id+"F0.wireOp",EDGE,"E12");var subQ87=sQuery(id+"F0.wireOp",EDGE,"E11");var subQ88=sQuery(id+"F0.wireOp",EDGE,"E10");var subQ89=sQuery(id+"F0.wireOp",EDGE,"E9.right");var subQ90=sQuery(id+"F0.wireOp",EDGE,"E9.left");var subQ91=sQuery(id+"F0.wireOp",EDGE,"E21.3");var subQ92=sQuery(id+"F0.wireOp",EDGE,"E9.top");var subQ93=sQuery(id+"F0.wireOp",EDGE,"E21.2");var subQ94=sQuery(id+"F0.wireOp",EDGE,"E9.bottom");var subQ95=sQuery(id+"F0.wireOp",EDGE,"E21.1");var subQ96=sQuery(id+"F0.wireOp",EDGE,"E8.right");var subQ97=sQuery(id+"F0.wireOp",EDGE,"E21.0");var subQ98=sQuery(id+"F0.wireOp",EDGE,"E8.left");var subQ99=sQuery(id+"F0.wireOp",EDGE,"E20.5");var subQ100=sQuery(id+"F0.wireOp",EDGE,"E8.top");var subQ101=sQuery(id+"F0.wireOp",EDGE,"E20.4");var subQ102=sQuery(id+"F0.wireOp",EDGE,"E8.bottom");var subQ103=sQuery(id+"F0.wireOp",EDGE,"E20.3");var subQ104=sQuery(id+"F0.wireOp",EDGE,"E7.right");var subQ105=sQuery(id+"F0.wireOp",EDGE,"E20.2");var subQ106=sQuery(id+"F0.wireOp",EDGE,"E7.left");var subQ107=sQuery(id+"F0.wireOp",EDGE,"E20.1");var subQ108=sQuery(id+"F0.wireOp",EDGE,"E7.top");var subQ109=sQuery(id+"F0.wireOp",EDGE,"E20.0");var subQ110=sQuery(id+"F0.wireOp",EDGE,"E7.bottom");var subQ111=sQuery(id+"F0.wireOp",EDGE,"E6.right");var subQ112=sQuery(id+"F0.wireOp",EDGE,"E6.left");var subQ113=sQuery(id+"F0.wireOp",EDGE,"E17");var subQ114=sQuery(id+"F0.wireOp",EDGE,"E6.top");var subQ115=sQuery(id+"F0.wireOp",EDGE,"E6.bottom");var subQ116=sQuery(id+"F0.wireOp",EDGE,"E5.right");var subQ117=sQuery(id+"F0.wireOp",EDGE,"E5.left");var subQ118=sQuery(id+"F0.wireOp",EDGE,"E2.bottom");var subQ119=sQuery(id+"F0.wireOp",EDGE,"E1.right");var subQ120=sQuery(id+"F0.wireOp",EDGE,"E1.left");var subQ121=sQuery(id+"F0.wireOp",EDGE,"E1.top");var subQ122=sQuery(id+"F0.wireOp",EDGE,"E1.bottom");var subQ123=sQuery(id+"F0.wireOp",EDGE,"E2.top");var subQ124=sQuery(id+"F0.wireOp",EDGE,"E15");var subQ125=sQuery(id+"F0.wireOp",EDGE,"E0.bottom");var subQ126=sQuery(id+"F0.wireOp",EDGE,"E27.3");var subQ127=sQuery(id+"F0.wireOp",EDGE,"E5.top");var subQ128=sQuery(id+"F0.wireOp",EDGE,"E0.right");var subQ129=sQuery(id+"F0.wireOp",EDGE,"E0.top");var subQ130=sQuery(id+"F0.wireOp",EDGE,"E0.left");var subQ131=sQuery(id+"F0.wireOp",EDGE,"E2.left");var subQ132=sQuery(id+"F0.wireOp",EDGE,"E2.right");var subQ133=sQuery(id+"F0.wireOp",EDGE,"E3.bottom");var subQ134=sQuery(id+"F0.wireOp",EDGE,"E3.top");var subQ135=sQuery(id+"F0.wireOp",EDGE,"E3.left");var subQ136=sQuery(id+"F0.wireOp",EDGE,"E3.right");var subQ137=sQuery(id+"F0.wireOp",EDGE,"E4.bottom");var subQ138=sQuery(id+"F0.wireOp",EDGE,"E4.top");var subQ139=sQuery(id+"F0.wireOp",EDGE,"E4.left");var subQ140=sQuery(id+"F0.wireOp",EDGE,"E4.right");var subQ141=sQuery(id+"F0.wireOp",EDGE,"E5.bottom");var subQ142=sQuery(id+"F0.wireOp",EDGE,"E16");var subQ143=sQuery(id+"F0.wireOp",EDGE,"E18");var subQ144=sQuery(id+"F0.wireOp",EDGE,"E19");var subQ145=sQuery(id+"F0.wireOp",EDGE,"E24.0");var subQ146=sQuery(id+"F0.wireOp",EDGE,"E24.3");var subQ147=sQuery(id+"F0.wireOp",EDGE,"E24.4");var subQ148=sQuery(id+"F0.wireOp",EDGE,"E24.5");var subQ149=sQuery(id+"F0.wireOp",EDGE,"E25.0");var subQ150=sQuery(id+"F0.wireOp",EDGE,"E25.1");var subQ151=sQuery(id+"F0.wireOp",EDGE,"E25.2");var subQ152=sQuery(id+"F0.wireOp",EDGE,"E21.4");var subQ153=sQuery(id+"F0.wireOp",EDGE,"E21.5");var subQ154=sQuery(id+"F0.wireOp",EDGE,"E22.0");var subQ155=sQuery(id+"F0.wireOp",EDGE,"E22.1");var subQ156=sQuery(id+"F0.wireOp",EDGE,"E22.2");var subQ157=sQuery(id+"F0.wireOp",EDGE,"E22.3");var subQ158=sQuery(id+"F0.wireOp",EDGE,"E22.4");var subQ159=sQuery(id+"F0.wireOp",EDGE,"E22.5");var subQ160=sQuery(id+"F0.wireOp",EDGE,"E23.0");var subQ161=sQuery(id+"F0.wireOp",EDGE,"E23.1");var subQ162=sQuery(id+"F0.wireOp",EDGE,"E23.2");var subQ163=sQuery(id+"F0.wireOp",EDGE,"E23.3");var subQ164=sQuery(id+"F0.wireOp",EDGE,"E23.4");var subQ165=sQuery(id+"F0.wireOp",EDGE,"E23.5");var subQ166=sQuery(id+"F0.wireOp",EDGE,"E24.1");var subQ167=sQuery(id+"F0.wireOp",EDGE,"E24.2");var subQ168=sQuery(id+"F0.wireOp",EDGE,"E25.3");var subQ169=sQuery(id+"F0.wireOp",EDGE,"E25.4");var subQ170=sQuery(id+"F0.wireOp",EDGE,"E25.5");var subQ171=sQuery(id+"F0.wireOp",EDGE,"E26.0");var subQ172=sQuery(id+"F0.wireOp",EDGE,"E26.1");var subQ173=sQuery(id+"F0.wireOp",EDGE,"E26.2");var subQ174=sQuery(id+"F0.wireOp",EDGE,"E26.3");var subQ175=sQuery(id+"F0.wireOp",EDGE,"E26.4");var subQ176=sQuery(id+"F0.wireOp",EDGE,"E26.5");var subQ177=sQuery(id+"F0.wireOp",EDGE,"E27.0");var subQ178=sQuery(id+"F0.wireOp",EDGE,"E27.1");var subQ179=sQuery(id+"F0.wireOp",EDGE,"E27.2");Q0=makeQuery(id+"F3.boolean.opBoolean","SPLIT",FACE,{"disambiguationData":[TD([makeQuery(id+"F1.opExtrude","SWEPT_FACE",FACE,{"disambiguationData":[OSD([subQ125])]})])],"derivedFrom":makeQuery(id+"F1.opExtrude","CAP_FACE",FACE,{"disambiguationData":[OSD([subQ125,subQ129,subQ130,subQ128,subQ122,subQ121,subQ120,subQ119,subQ118,subQ123,subQ131,subQ132,subQ133,subQ134,subQ135,subQ136,subQ137,subQ138,subQ139,subQ140,subQ141,subQ127,subQ117,subQ116,subQ115,subQ114,subQ112,subQ111,subQ110,subQ108,subQ106,subQ104,subQ102,subQ100,subQ98,subQ96,subQ94,subQ92,subQ90,subQ89,subQ88,subQ87,subQ86,subQ85,subQ84,subQ124,subQ142,subQ113,subQ143,subQ144,subQ109,subQ107,subQ105,subQ103,subQ101,subQ99,subQ97,subQ95,subQ93,subQ91,subQ152,subQ153,subQ154,subQ155,subQ156,subQ157,subQ158,subQ159,subQ160,subQ161,subQ162,subQ163,subQ164,subQ165,subQ145,subQ166,subQ167,subQ146,subQ147,subQ148,subQ149,subQ150,subQ151,subQ168,subQ169,subQ170,subQ171,subQ172,subQ173,subQ174,subQ175,subQ176,subQ177,subQ178,subQ179,subQ126,subQ83,subQ82,subQ81,subQ80,subQ79,subQ78,subQ77,subQ76,subQ75,subQ74,subQ73,subQ72,subQ71,subQ70,subQ69,subQ68,subQ67,subQ66,subQ65,subQ64,subQ63,subQ62,subQ61,subQ60,subQ59,subQ58,subQ57,subQ56,subQ55,subQ54,subQ53,subQ52,subQ51,subQ50,subQ49,subQ48,subQ47,subQ46,subQ45,subQ44,subQ43,subQ42,subQ41,subQ40,subQ39,subQ38,subQ37,subQ36,subQ35,subQ34,subQ33,subQ32,subQ31,subQ30,subQ29,subQ28,subQ27,subQ26,subQ25,subQ24,subQ23,subQ22,subQ21,subQ20,subQ19,subQ18,subQ17,subQ16,subQ15,subQ14,subQ13,subQ12,subQ11,subQ10,subQ9,subQ8,subQ7,subQ6,subQ5,subQ4,subQ3,subQ2,subQ1,subQ0])],"isStart":false})});}
            var sketch = newSketch(context, id + "F4", { "sketchPlane" : qUnion([Q0])});
            skText(sketch, "E52", { "text": "q-_-p", "fontName": "OpenSans-Bold.ttf"});
            const initialGuessF4  = {"E52": [0, -0.0043, 1, 0, 0.0043]};
            skSetInitialGuess(sketch, initialGuessF4);
            skSolve(sketch);
        }
        {
            var Q0;
            {var subQ0=sQuery(id+"F0.wireOp",EDGE,"E38.0");var subQ1=sQuery(id+"F0.wireOp",EDGE,"E37.2");var subQ2=sQuery(id+"F0.wireOp",EDGE,"E37.1");var subQ3=sQuery(id+"F0.wireOp",EDGE,"E37.0");var subQ4=sQuery(id+"F0.wireOp",EDGE,"E36.2");var subQ6=sQuery(id+"F0.wireOp",EDGE,"E36.1");var subQ8=sQuery(id+"F0.wireOp",EDGE,"E36.0");var subQ10=sQuery(id+"F0.wireOp",EDGE,"E35.2");var subQ11=sQuery(id+"F0.wireOp",EDGE,"E35.1");var subQ12=sQuery(id+"F0.wireOp",EDGE,"E35.0");var subQ13=sQuery(id+"F0.wireOp",EDGE,"E34.2");var subQ14=sQuery(id+"F0.wireOp",EDGE,"E34.1");var subQ15=sQuery(id+"F0.wireOp",EDGE,"E34.0");var subQ16=sQuery(id+"F0.wireOp",EDGE,"E33.2");var subQ17=sQuery(id+"F0.wireOp",EDGE,"E33.1");var subQ19=sQuery(id+"F0.wireOp",EDGE,"E33.0");var subQ21=sQuery(id+"F0.wireOp",EDGE,"E32.2");var subQ23=sQuery(id+"F0.wireOp",EDGE,"E32.1");var subQ25=sQuery(id+"F0.wireOp",EDGE,"E32.0");var subQ26=sQuery(id+"F0.wireOp",EDGE,"E31.2");var subQ28=sQuery(id+"F0.wireOp",EDGE,"E31.1");var subQ29=sQuery(id+"F0.wireOp",EDGE,"E31.0");var subQ30=sQuery(id+"F0.wireOp",EDGE,"E30.2");var subQ32=sQuery(id+"F0.wireOp",EDGE,"E30.1");var subQ34=sQuery(id+"F0.wireOp",EDGE,"E30.0");var subQ36=sQuery(id+"F0.wireOp",EDGE,"E29.5");var subQ38=sQuery(id+"F0.wireOp",EDGE,"E29.4");var subQ39=sQuery(id+"F0.wireOp",EDGE,"E29.3");var subQ41=sQuery(id+"F0.wireOp",EDGE,"E29.2");var subQ42=sQuery(id+"F0.wireOp",EDGE,"E29.1");var subQ44=sQuery(id+"F0.wireOp",EDGE,"E29.0");var subQ46=sQuery(id+"F0.wireOp",EDGE,"E28.5");var subQ48=sQuery(id+"F0.wireOp",EDGE,"E28.4");var subQ50=sQuery(id+"F0.wireOp",EDGE,"E28.3");var subQ52=sQuery(id+"F0.wireOp",EDGE,"E28.2");var subQ54=sQuery(id+"F0.wireOp",EDGE,"E28.1");var subQ56=sQuery(id+"F0.wireOp",EDGE,"E28.0");var subQ58=sQuery(id+"F0.wireOp",EDGE,"E27.5");var subQ60=sQuery(id+"F0.wireOp",EDGE,"E27.4");var subQ62=sQuery(id+"F0.wireOp",EDGE,"E27.3");var subQ64=sQuery(id+"F0.wireOp",EDGE,"E27.2");var subQ65=sQuery(id+"F0.wireOp",EDGE,"E27.1");var subQ66=sQuery(id+"F0.wireOp",EDGE,"E27.0");var subQ67=sQuery(id+"F0.wireOp",EDGE,"E26.5");var subQ68=sQuery(id+"F0.wireOp",EDGE,"E26.4");var subQ69=sQuery(id+"F0.wireOp",EDGE,"E26.3");var subQ70=sQuery(id+"F0.wireOp",EDGE,"E26.2");var subQ71=sQuery(id+"F0.wireOp",EDGE,"E26.1");var subQ72=sQuery(id+"F0.wireOp",EDGE,"E26.0");var subQ73=sQuery(id+"F0.wireOp",EDGE,"E21.4");var subQ74=sQuery(id+"F0.wireOp",EDGE,"E21.3");var subQ75=sQuery(id+"F0.wireOp",EDGE,"E21.2");var subQ76=sQuery(id+"F0.wireOp",EDGE,"E21.1");var subQ77=sQuery(id+"F0.wireOp",EDGE,"E21.0");var subQ78=sQuery(id+"F0.wireOp",EDGE,"E20.5");var subQ79=sQuery(id+"F0.wireOp",EDGE,"E20.4");var subQ80=sQuery(id+"F0.wireOp",EDGE,"E20.3");var subQ81=sQuery(id+"F0.wireOp",EDGE,"E20.2");var subQ82=sQuery(id+"F0.wireOp",EDGE,"E20.1");var subQ83=sQuery(id+"F0.wireOp",EDGE,"E20.0");var subQ84=sQuery(id+"F0.wireOp",EDGE,"E12");var subQ85=sQuery(id+"F0.wireOp",EDGE,"E11");var subQ86=sQuery(id+"F0.wireOp",EDGE,"E13");var subQ87=sQuery(id+"F0.wireOp",EDGE,"E21.5");var subQ88=sQuery(id+"F0.wireOp",EDGE,"E38.1");var subQ89=sQuery(id+"F0.wireOp",EDGE,"E10");var subQ90=sQuery(id+"F0.wireOp",EDGE,"E25.5");var subQ91=sQuery(id+"F0.wireOp",EDGE,"E19");var subQ92=sQuery(id+"F0.wireOp",EDGE,"E14");var subQ93=sQuery(id+"F0.wireOp",EDGE,"E15");var subQ94=sQuery(id+"F0.wireOp",EDGE,"E16");var subQ95=sQuery(id+"F0.wireOp",EDGE,"E17");var subQ96=sQuery(id+"F0.wireOp",EDGE,"E18");var subQ97=sQuery(id+"F0.wireOp",EDGE,"E22.0");var subQ98=sQuery(id+"F0.wireOp",EDGE,"E22.1");var subQ99=sQuery(id+"F0.wireOp",EDGE,"E22.2");var subQ100=sQuery(id+"F0.wireOp",EDGE,"E22.3");var subQ102=sQuery(id+"F0.wireOp",EDGE,"E22.4");var subQ112=sQuery(id+"F0.wireOp",EDGE,"E22.5");var subQ113=sQuery(id+"F0.wireOp",EDGE,"E23.0");var subQ114=sQuery(id+"F0.wireOp",EDGE,"E23.1");var subQ115=sQuery(id+"F0.wireOp",EDGE,"E23.2");var subQ116=sQuery(id+"F0.wireOp",EDGE,"E23.3");var subQ117=sQuery(id+"F0.wireOp",EDGE,"E23.4");var subQ118=sQuery(id+"F0.wireOp",EDGE,"E23.5");var subQ119=sQuery(id+"F0.wireOp",EDGE,"E24.0");var subQ120=sQuery(id+"F0.wireOp",EDGE,"E24.1");var subQ121=sQuery(id+"F0.wireOp",EDGE,"E24.2");var subQ122=sQuery(id+"F0.wireOp",EDGE,"E24.3");var subQ123=sQuery(id+"F0.wireOp",EDGE,"E24.4");var subQ124=sQuery(id+"F0.wireOp",EDGE,"E24.5");var subQ125=sQuery(id+"F0.wireOp",EDGE,"E25.0");var subQ126=sQuery(id+"F0.wireOp",EDGE,"E25.1");var subQ127=sQuery(id+"F0.wireOp",EDGE,"E25.2");var subQ128=sQuery(id+"F0.wireOp",EDGE,"E25.3");var subQ129=sQuery(id+"F0.wireOp",EDGE,"E25.4");var subQ130=sQuery(id+"F0.wireOp",EDGE,"E38.2");var subQ131=sQuery(id+"F0.wireOp",EDGE,"E39.0");var subQ133=sQuery(id+"F0.wireOp",EDGE,"E39.1");var subQ136=sQuery(id+"F0.wireOp",EDGE,"E39.2");var subQ137=sQuery(id+"F0.wireOp",EDGE,"E41.bottom");var subQ138=sQuery(id+"F0.wireOp",EDGE,"E41.top");var subQ139=sQuery(id+"F0.wireOp",EDGE,"E41.left");var subQ140=sQuery(id+"F0.wireOp",EDGE,"E41.right");var subQ141=sQuery(id+"F0.wireOp",EDGE,"E42.bottom");var subQ148=sQuery(id+"F0.wireOp",EDGE,"E42.top");var subQ149=sQuery(id+"F0.wireOp",EDGE,"E42.left");var subQ150=sQuery(id+"F0.wireOp",EDGE,"E42.right");var subQ151=sQuery(id+"F0.wireOp",EDGE,"E43.bottom");var subQ152=sQuery(id+"F0.wireOp",EDGE,"E43.top");var subQ153=sQuery(id+"F0.wireOp",EDGE,"E43.left");var subQ154=sQuery(id+"F0.wireOp",EDGE,"E43.right");var subQ155=sQuery(id+"F0.wireOp",EDGE,"E44.bottom");var subQ156=sQuery(id+"F0.wireOp",EDGE,"E44.top");var subQ157=sQuery(id+"F0.wireOp",EDGE,"E44.left");var subQ158=sQuery(id+"F0.wireOp",EDGE,"E44.right");var subQ159=sQuery(id+"F0.wireOp",EDGE,"E45.bottom");var subQ160=sQuery(id+"F0.wireOp",EDGE,"E45.top");var subQ161=sQuery(id+"F0.wireOp",EDGE,"E45.left");var subQ162=sQuery(id+"F0.wireOp",EDGE,"E45.right");var subQ163=sQuery(id+"F0.wireOp",EDGE,"E46.bottom");var subQ164=sQuery(id+"F0.wireOp",EDGE,"E46.top");var subQ165=sQuery(id+"F0.wireOp",EDGE,"E46.left");var subQ166=sQuery(id+"F0.wireOp",EDGE,"E46.right");var subQ167=sQuery(id+"F0.wireOp",EDGE,"E47.bottom");var subQ168=sQuery(id+"F0.wireOp",EDGE,"E47.top");var subQ169=sQuery(id+"F0.wireOp",EDGE,"E47.left");var subQ170=sQuery(id+"F0.wireOp",EDGE,"E47.right");var subQ171=sQuery(id+"F0.wireOp",EDGE,"E48.bottom");var subQ172=sQuery(id+"F0.wireOp",EDGE,"E48.top");var subQ173=sQuery(id+"F0.wireOp",EDGE,"E48.left");var subQ174=sQuery(id+"F0.wireOp",EDGE,"E48.right");var subQ175=sQuery(id+"F0.wireOp",EDGE,"E49.bottom");var subQ176=sQuery(id+"F0.wireOp",EDGE,"E49.top");var subQ177=sQuery(id+"F0.wireOp",EDGE,"E49.left");var subQ178=sQuery(id+"F0.wireOp",EDGE,"E49.right");var subQ179=sQuery(id+"F0.wireOp",EDGE,"E50.bottom");var subQ180=sQuery(id+"F0.wireOp",EDGE,"E50.top");var subQ181=sQuery(id+"F0.wireOp",EDGE,"E50.left");var subQ182=sQuery(id+"F0.wireOp",EDGE,"E50.right");Q0=makeQuery(id+"F3.boolean.opBoolean","SPLIT",FACE,{"disambiguationData":[TD([makeQuery(id+"F1.opExtrude","SWEPT_FACE",FACE,{"disambiguationData":[OSD([subQ89])]})])],"derivedFrom":makeQuery(id+"F1.opExtrude","CAP_FACE",FACE,{"disambiguationData":[OSD([subQ89,subQ85,subQ84,subQ86,subQ92,subQ93,subQ94,subQ95,subQ96,subQ91,subQ83,subQ82,subQ81,subQ80,subQ79,subQ78,subQ77,subQ76,subQ75,subQ74,subQ73,subQ87,subQ97,subQ98,subQ99,subQ100,subQ102,subQ112,subQ113,subQ114,subQ115,subQ116,subQ117,subQ118,subQ119,subQ120,subQ121,subQ122,subQ123,subQ124,subQ125,subQ126,subQ127,subQ128,subQ129,subQ90,subQ72,subQ71,subQ70,subQ69,subQ68,subQ67,subQ66,subQ65,subQ64,subQ62,subQ60,subQ58,subQ56,subQ54,subQ52,subQ50,subQ48,subQ46,subQ44,subQ42,subQ41,subQ39,subQ38,subQ36,subQ34,subQ32,subQ30,subQ29,subQ28,subQ26,subQ25,subQ23,subQ21,subQ19,subQ17,subQ16,subQ15,subQ14,subQ13,subQ12,subQ11,subQ10,subQ8,subQ6,subQ4,subQ3,subQ2,subQ1,subQ0,subQ88,subQ130,subQ131,subQ133,subQ136,subQ137,subQ138,subQ139,subQ140,subQ141,subQ148,subQ149,subQ150,subQ151,subQ152,subQ153,subQ154,subQ155,subQ156,subQ157,subQ158,subQ159,subQ160,subQ161,subQ162,subQ163,subQ164,subQ165,subQ166,subQ167,subQ168,subQ169,subQ170,subQ171,subQ172,subQ173,subQ174,subQ175,subQ176,subQ177,subQ178,subQ179,subQ180,subQ181,subQ182])],"isStart":false})});}
            var sketch = newSketch(context, id + "F5", { "sketchPlane" : qUnion([Q0])});
            skLineSegment(sketch, "E53.bottom", {"start": v(-1, 80.61) * mm, "end": v(0, 80.61) * mm});
            skLineSegment(sketch, "E53.top", {"start": v(-1, 75.61) * mm, "end": v(0, 75.61) * mm});
            skLineSegment(sketch, "E53.left", {"start": v(-1, 80.61) * mm, "end": v(-1, 75.61) * mm});
            skLineSegment(sketch, "E53.right", {"start": v(0, 80.61) * mm, "end": v(0, 75.61) * mm});
            skLineSegment(sketch, "E54.bottom", {"start": v(9, 80.61) * mm, "end": v(10, 80.61) * mm});
            skLineSegment(sketch, "E54.top", {"start": v(9, 78.11) * mm, "end": v(10, 78.11) * mm});
            skLineSegment(sketch, "E54.left", {"start": v(9, 80.61) * mm, "end": v(9, 78.11) * mm});
            skLineSegment(sketch, "E54.right", {"start": v(10, 80.61) * mm, "end": v(10, 78.11) * mm});
            skLineSegment(sketch, "E55.bottom", {"start": v(19, 80.61) * mm, "end": v(20, 80.61) * mm});
            skLineSegment(sketch, "E55.top", {"start": v(19, 78.11) * mm, "end": v(20, 78.11) * mm});
            skLineSegment(sketch, "E55.left", {"start": v(19, 80.61) * mm, "end": v(19, 78.11) * mm});
            skLineSegment(sketch, "E55.right", {"start": v(20, 80.61) * mm, "end": v(20, 78.11) * mm});
            skLineSegment(sketch, "E56.bottom", {"start": v(29, 80.61) * mm, "end": v(30, 80.61) * mm});
            skLineSegment(sketch, "E56.top", {"start": v(29, 78.11) * mm, "end": v(30, 78.11) * mm});
            skLineSegment(sketch, "E56.left", {"start": v(29, 80.61) * mm, "end": v(29, 78.11) * mm});
            skLineSegment(sketch, "E56.right", {"start": v(30, 80.61) * mm, "end": v(30, 78.11) * mm});
            skLineSegment(sketch, "E57.bottom", {"start": v(39, 80.61) * mm, "end": v(40, 80.61) * mm});
            skLineSegment(sketch, "E57.top", {"start": v(39, 78.11) * mm, "end": v(40, 78.11) * mm});
            skLineSegment(sketch, "E57.left", {"start": v(39, 80.61) * mm, "end": v(39, 78.11) * mm});
            skLineSegment(sketch, "E57.right", {"start": v(40, 80.61) * mm, "end": v(40, 78.11) * mm});
            skLineSegment(sketch, "E58.bottom", {"start": v(49, 80.61) * mm, "end": v(50, 80.61) * mm});
            skLineSegment(sketch, "E58.top", {"start": v(49, 75.61) * mm, "end": v(50, 75.61) * mm});
            skLineSegment(sketch, "E58.left", {"start": v(49, 80.61) * mm, "end": v(49, 75.61) * mm});
            skLineSegment(sketch, "E58.right", {"start": v(50, 80.61) * mm, "end": v(50, 75.61) * mm});
            skLineSegment(sketch, "E59.bottom", {"start": v(59, 80.61) * mm, "end": v(60, 80.61) * mm});
            skLineSegment(sketch, "E59.top", {"start": v(59, 78.11) * mm, "end": v(60, 78.11) * mm});
            skLineSegment(sketch, "E59.left", {"start": v(59, 80.61) * mm, "end": v(59, 78.11) * mm});
            skLineSegment(sketch, "E59.right", {"start": v(60, 80.61) * mm, "end": v(60, 78.11) * mm});
            skLineSegment(sketch, "E60.bottom", {"start": v(69, 80.61) * mm, "end": v(70, 80.61) * mm});
            skLineSegment(sketch, "E60.top", {"start": v(69, 78.11) * mm, "end": v(70, 78.11) * mm});
            skLineSegment(sketch, "E60.left", {"start": v(69, 80.61) * mm, "end": v(69, 78.11) * mm});
            skLineSegment(sketch, "E60.right", {"start": v(70, 80.61) * mm, "end": v(70, 78.11) * mm});
            skLineSegment(sketch, "E61.bottom", {"start": v(79, 80.61) * mm, "end": v(80, 80.61) * mm});
            skLineSegment(sketch, "E61.top", {"start": v(79, 78.11) * mm, "end": v(80, 78.11) * mm});
            skLineSegment(sketch, "E61.left", {"start": v(79, 80.61) * mm, "end": v(79, 78.11) * mm});
            skLineSegment(sketch, "E61.right", {"start": v(80, 80.61) * mm, "end": v(80, 78.11) * mm});
            skLineSegment(sketch, "E62.bottom", {"start": v(89, 80.61) * mm, "end": v(90, 80.61) * mm});
            skLineSegment(sketch, "E62.top", {"start": v(89, 78.11) * mm, "end": v(90, 78.11) * mm});
            skLineSegment(sketch, "E62.left", {"start": v(89, 80.61) * mm, "end": v(89, 78.11) * mm});
            skLineSegment(sketch, "E62.right", {"start": v(90, 80.61) * mm, "end": v(90, 78.11) * mm});
            skLineSegment(sketch, "E63.bottom", {"start": v(99, 80.61) * mm, "end": v(100, 80.61) * mm});
            skLineSegment(sketch, "E63.top", {"start": v(99, 75.61) * mm, "end": v(100, 75.61) * mm});
            skLineSegment(sketch, "E63.left", {"start": v(99, 80.61) * mm, "end": v(99, 75.61) * mm});
            skLineSegment(sketch, "E63.right", {"start": v(100, 80.61) * mm, "end": v(100, 75.61) * mm});
            skLineSegment(sketch, "E64.bottom", {"start": v(109, 80.61) * mm, "end": v(110, 80.61) * mm});
            skLineSegment(sketch, "E64.top", {"start": v(109, 78.11) * mm, "end": v(110, 78.11) * mm});
            skLineSegment(sketch, "E64.left", {"start": v(109, 80.61) * mm, "end": v(109, 78.11) * mm});
            skLineSegment(sketch, "E64.right", {"start": v(110, 80.61) * mm, "end": v(110, 78.11) * mm});
            skLineSegment(sketch, "E65.bottom", {"start": v(119, 80.61) * mm, "end": v(120, 80.61) * mm});
            skLineSegment(sketch, "E65.top", {"start": v(119, 78.11) * mm, "end": v(120, 78.11) * mm});
            skLineSegment(sketch, "E65.left", {"start": v(119, 80.61) * mm, "end": v(119, 78.11) * mm});
            skLineSegment(sketch, "E65.right", {"start": v(120, 80.61) * mm, "end": v(120, 78.11) * mm});
            skLineSegment(sketch, "E66.bottom", {"start": v(129, 80.61) * mm, "end": v(130, 80.61) * mm});
            skLineSegment(sketch, "E66.top", {"start": v(129, 78.11) * mm, "end": v(130, 78.11) * mm});
            skLineSegment(sketch, "E66.left", {"start": v(129, 80.61) * mm, "end": v(129, 78.11) * mm});
            skLineSegment(sketch, "E66.right", {"start": v(130, 80.61) * mm, "end": v(130, 78.11) * mm});
            skLineSegment(sketch, "E67.bottom", {"start": v(139, 80.61) * mm, "end": v(140, 80.61) * mm});
            skLineSegment(sketch, "E67.top", {"start": v(139, 78.11) * mm, "end": v(140, 78.11) * mm});
            skLineSegment(sketch, "E67.left", {"start": v(139, 80.61) * mm, "end": v(139, 78.11) * mm});
            skLineSegment(sketch, "E67.right", {"start": v(140, 80.61) * mm, "end": v(140, 78.11) * mm});
            skLineSegment(sketch, "E68.bottom", {"start": v(149, 80.61) * mm, "end": v(150, 80.61) * mm});
            skLineSegment(sketch, "E68.top", {"start": v(149, 75.61) * mm, "end": v(150, 75.61) * mm});
            skLineSegment(sketch, "E68.left", {"start": v(149, 80.61) * mm, "end": v(149, 75.61) * mm});
            skLineSegment(sketch, "E68.right", {"start": v(150, 80.61) * mm, "end": v(150, 75.61) * mm});
            skLineSegment(sketch, "E69.bottom", {"start": v(159, 80.61) * mm, "end": v(160, 80.61) * mm});
            skLineSegment(sketch, "E69.top", {"start": v(159, 78.11) * mm, "end": v(160, 78.11) * mm});
            skLineSegment(sketch, "E69.left", {"start": v(159, 80.61) * mm, "end": v(159, 78.11) * mm});
            skLineSegment(sketch, "E69.right", {"start": v(160, 80.61) * mm, "end": v(160, 78.11) * mm});
            skLineSegment(sketch, "E70.bottom", {"start": v(169, 80.61) * mm, "end": v(170, 80.61) * mm});
            skLineSegment(sketch, "E70.top", {"start": v(169, 78.11) * mm, "end": v(170, 78.11) * mm});
            skLineSegment(sketch, "E70.left", {"start": v(169, 80.61) * mm, "end": v(169, 78.11) * mm});
            skLineSegment(sketch, "E70.right", {"start": v(170, 80.61) * mm, "end": v(170, 78.11) * mm});
            skLineSegment(sketch, "E71.bottom", {"start": v(179, 80.61) * mm, "end": v(180, 80.61) * mm});
            skLineSegment(sketch, "E71.top", {"start": v(179, 78.11) * mm, "end": v(180, 78.11) * mm});
            skLineSegment(sketch, "E71.left", {"start": v(179, 80.61) * mm, "end": v(179, 78.11) * mm});
            skLineSegment(sketch, "E71.right", {"start": v(180, 80.61) * mm, "end": v(180, 78.11) * mm});
            skLineSegment(sketch, "E72.bottom", {"start": v(189, 80.61) * mm, "end": v(190, 80.61) * mm});
            skLineSegment(sketch, "E72.top", {"start": v(189, 78.11) * mm, "end": v(190, 78.11) * mm});
            skLineSegment(sketch, "E72.left", {"start": v(189, 80.61) * mm, "end": v(189, 78.11) * mm});
            skLineSegment(sketch, "E72.right", {"start": v(190, 80.61) * mm, "end": v(190, 78.11) * mm});
            skLineSegment(sketch, "E73.bottom", {"start": v(199, 80.61) * mm, "end": v(200, 80.61) * mm});
            skLineSegment(sketch, "E73.top", {"start": v(199, 75.61) * mm, "end": v(200, 75.61) * mm});
            skLineSegment(sketch, "E73.left", {"start": v(199, 80.61) * mm, "end": v(199, 75.61) * mm});
            skLineSegment(sketch, "E73.right", {"start": v(200, 80.61) * mm, "end": v(200, 75.61) * mm});
            skLineSegment(sketch, "E74", {"start": v(-6, 70.61) * mm, "end": v(205, 70.61) * mm});
            skText(sketch, "E75", { "text": "0", "fontName": "OpenSans-Bold.ttf"});
            skText(sketch, "E76", { "text": "5", "fontName": "OpenSans-Bold.ttf"});
            skText(sketch, "E77", { "text": "10", "fontName": "OpenSans-Regular.ttf"});
            skText(sketch, "E78", { "text": "15", "fontName": "OpenSans-Bold.ttf"});
            skText(sketch, "E79", { "text": "20", "fontName": "OpenSans-Bold.ttf"});
            const initialGuessF5  = {"E75": [-0.002, 0.07061, 1, 0, 0.004], "E76": [0.048, 0.07061, 1, 0, 0.004], "E77": [0.0965, 0.07061, 1, 0, 0.004], "E78": [0.1465, 0.07061, 1, 0, 0.004], "E79": [0.1975, 0.07061, 1, 0, 0.004]};
            skSetInitialGuess(sketch, initialGuessF5);
            skSolve(sketch);
        }
        {
            var Q0;
            Q0=qSketchRegion(id+"F5",true);
            extrude(context, id + "F6", {"entities" : qUnion([Q0]), "operationType" : NewBodyOperationType.ADD, "depth" : .4 * mm, "offsetDistance" : 25 * mm});
        }
    });
